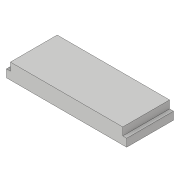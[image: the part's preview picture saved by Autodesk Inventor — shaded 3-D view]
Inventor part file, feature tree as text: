
AUTODESK INVENTOR PART (.ipt)
format: ipt  version: 2018.3 (Build 223284000, 284)  size: 96,256 bytes
history: native  units: in
note: dims shown in document units (in); Inventor stores cm internally (conversion verified against a paired STEP export)
features: extrude x2, sketch x2
ambient origin geometry x8: Origin, YZ Plane, XZ Plane, XY Plane, X Axis, Y Axis, Z Axis, Center Point
bodies: Solid1 (feature_tree)
feature tree (4):
  extrude  "Extrusion1"  Depth=0.75in
  extrude  "Extrusion5"  Depth=0.0625in
  sketch  "Sketch1"  dims[d0=1.925in d1=0.75in]
  sketch  "Sketch5"  dims[d2=0.25in d3=0.0in d17=0.0625in d18=0.0625in d19=0.125in d20=0.0in]
